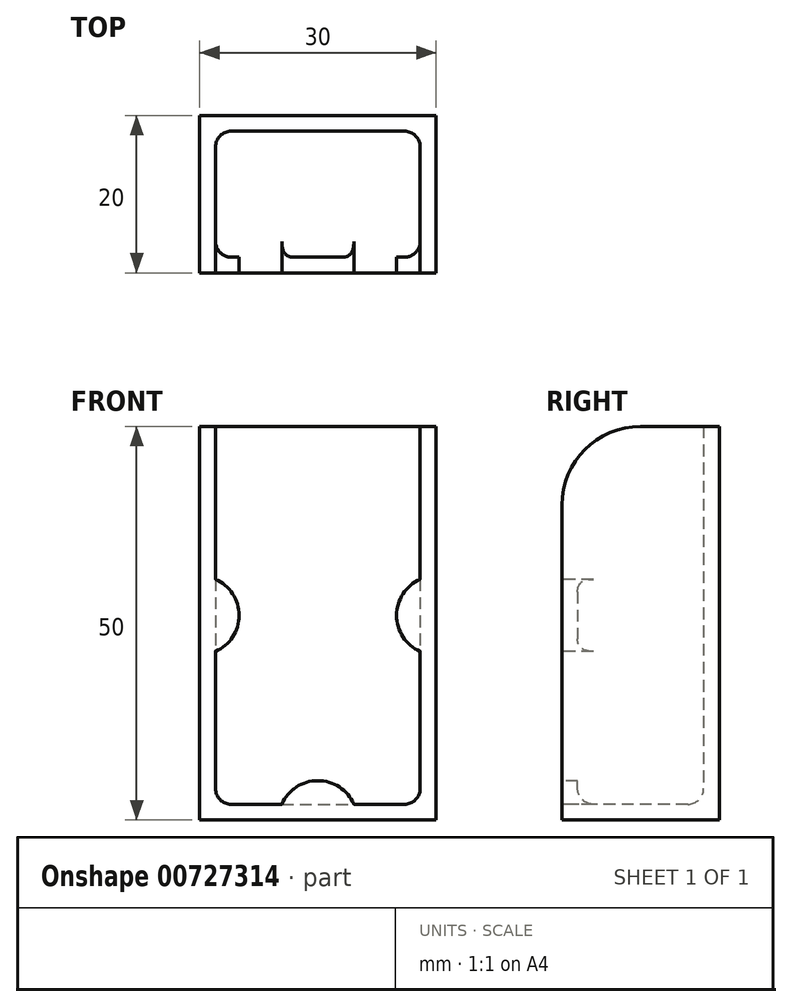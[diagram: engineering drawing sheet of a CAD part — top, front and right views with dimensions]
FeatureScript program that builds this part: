
annotation { "Feature Type Name" : "Feature", "Feature Type Description" : "" }
export const myFeature = defineFeature(function(context is Context, id is Id, definition is map)
    precondition{}
    {
        {
            var Q0;
            Q0=qCreatedBy(makeId("Top.planeOp"),FACE);
            var sketch = newSketch(context, id + "F0", { "sketchPlane" : qUnion([Q0])});
            skLineSegment(sketch, "E0.bottom", {"start": v(-15, 10) * mm, "end": v(15, 10) * mm});
            skLineSegment(sketch, "E0.top", {"start": v(-15, -10) * mm, "end": v(15, -10) * mm});
            skLineSegment(sketch, "E0.left", {"start": v(-15, 10) * mm, "end": v(-15, -10) * mm});
            skLineSegment(sketch, "E0.right", {"start": v(15, 10) * mm, "end": v(15, -10) * mm});
            skPoint(sketch, "E0.middle", {"position": v(0, 0) * mm});
            skLineSegment(sketch, "E1.bottom", {"start": v(-13, 8) * mm, "end": v(13, 8) * mm});
            skLineSegment(sketch, "E1.top", {"start": v(-13, -8) * mm, "end": v(13, -8) * mm});
            skLineSegment(sketch, "E1.left", {"start": v(-13, 8) * mm, "end": v(-13, -8) * mm});
            skLineSegment(sketch, "E1.right", {"start": v(13, 8) * mm, "end": v(13, -8) * mm});
            skSolve(sketch);
        }
        {
            var Q0;
            Q0=makeQuery(id+"F0.imprint","IMPRINT",FACE,{"disambiguationData":[TD([[makeQuery(id+"F0.imprint","IMPRINT",EDGE,{"derivedFrom":sQuery(id+"F0.wireOp",EDGE,"E0.bottom")}),-1.0]])]});
            extrude(context, id + "F1", {"entities" : qUnion([Q0]), "depth" : 50 * mm, "offsetDistance" : 25 * mm});
        }
        {
            var Q0;
            Q0=qCreatedBy(makeId("Top.planeOp"),FACE);
            var sketch = newSketch(context, id + "F2", { "sketchPlane" : qUnion([Q0])});
            skLineSegment(sketch, "E2.0", {"start": v(-15, 10) * mm, "end": v(-15, -10) * mm});
            skLineSegment(sketch, "E3.0", {"start": v(-15, -10) * mm, "end": v(15, -10) * mm});
            skLineSegment(sketch, "E4.0", {"start": v(15, 10) * mm, "end": v(15, -10) * mm});
            skLineSegment(sketch, "E5.0", {"start": v(-15, 10) * mm, "end": v(15, 10) * mm});
            skPoint(sketch, "E6.middle", {"position": v(0, 0) * mm});
            skSolve(sketch);
        }
        {
            var Q0;
            Q0=qSketchRegion(id+"F2",true);
            extrude(context, id + "F3", {"entities" : qUnion([Q0]), "operationType" : NewBodyOperationType.ADD, "depth" : 2 * mm, "offsetDistance" : 25 * mm});
        }
        {
            var Q0;
            Q0=makeQuery(id+"F1.opExtrude","SWEPT_FACE",FACE,{"disambiguationData":[OSD([sQuery(id+"F0.wireOp",EDGE,"E0.top")])]});
            var sketch = newSketch(context, id + "F4", { "sketchPlane" : qUnion([Q0])});
            skLineSegment(sketch, "E7.0", {"start": v(-13, 50) * mm, "end": v(13, 50) * mm});
            skLineSegment(sketch, "E8.0", {"start": v(-13, 2) * mm, "end": v(-4.58, 2) * mm});
            skLineSegment(sketch, "E9.0", {"start": v(13, 50) * mm, "end": v(13, 30.58) * mm});
            skLineSegment(sketch, "E10.0", {"start": v(-13, 50) * mm, "end": v(-13, 30.58) * mm});
            skArc(sketch, "E11", {"start": v(-13, 21.42) * mm, "mid": v(-10, 26) * mm, "end": v(-13, 30.58) * mm});
            skPoint(sketch, "E11.centerSnap0", {"position": v(-13, 26) * mm});
            skArc(sketch, "E12", {"start": v(4.58, 2) * mm, "mid": v(0, 5) * mm, "end": v(-4.58, 2) * mm});
            skArc(sketch, "E13", {"start": v(13, 30.58) * mm, "mid": v(10, 26) * mm, "end": v(13, 21.42) * mm});
            skPoint(sketch, "E13.centerSnap0", {"position": v(13, 26) * mm});
            skLineSegment(sketch, "E14.trimOffspring", {"start": v(13, 21.42) * mm, "end": v(13, 2) * mm});
            skLineSegment(sketch, "E15.trimOffspring", {"start": v(-13, 21.42) * mm, "end": v(-13, 2) * mm});
            skPoint(sketch, "E16.orphan", {"position": v(15, 50) * mm});
            skLineSegment(sketch, "E17.trimOffspring", {"start": v(4.58, 2) * mm, "end": v(13, 2) * mm});
            skPoint(sketch, "E18.0.end.orphan", {"position": v(15, 0) * mm});
            skPoint(sketch, "E19.orphan", {"position": v(-15, 0) * mm});
            skPoint(sketch, "E20.orphan", {"position": v(-15, 50) * mm});
            skSolve(sketch);
        }
        {
            var Q0;
            Q0=makeQuery(id+"F4.imprint","IMPRINT",FACE,{"disambiguationData":[TD([[makeQuery(id+"F4.imprint","IMPRINT",EDGE,{"derivedFrom":sQuery(id+"F4.wireOp",EDGE,"E7.0")}),-1.0]])]});
            extrude(context, id + "F5", {"entities" : qUnion([Q0]), "operationType" : NewBodyOperationType.REMOVE, "endBound" : BoundingType.UP_TO_NEXT, "oppositeDirection" : true, "depth" : 25 * mm, "offsetDistance" : 25 * mm});
        }
        {
            var Q0;
            {var subQ1=sQuery(id+"F0.wireOp",EDGE,"E0.right");var subQ2=sQuery(id+"F0.wireOp",EDGE,"E0.top");Q0=makeQuery(id+"F5.boolean.opBoolean","SPLIT",EDGE,{"disambiguationData":[TD([makeQuery(id+"F1.opExtrude","SWEPT_FACE",FACE,{"disambiguationData":[OSD([subQ1])]})])],"derivedFrom":makeQuery(id+"F1.opExtrude","CAP_EDGE",EDGE,{"disambiguationData":[OSD([subQ2])],"isStart":false})});}
            var Q1;
            {var subQ0=sQuery(id+"F0.wireOp",EDGE,"E0.left");var subQ2=sQuery(id+"F0.wireOp",EDGE,"E0.top");Q1=makeQuery(id+"F5.boolean.opBoolean","SPLIT",EDGE,{"disambiguationData":[TD([makeQuery(id+"F1.opExtrude","SWEPT_FACE",FACE,{"disambiguationData":[OSD([subQ0])]})])],"derivedFrom":makeQuery(id+"F1.opExtrude","CAP_EDGE",EDGE,{"disambiguationData":[OSD([subQ2])],"isStart":false})});}
            fillet(context, id + "F6", {"entities" : qUnion([Q0, Q1]), "radius" : 10 * mm, "tangentPropagation" : true, "allowEdgeOverflow" : false});
        }
        {
            var Q0;
            Q0=makeQuery(id+"F5.boolean.opBoolean","MERGE",EDGE,{"derivedFrom":[makeQuery(id+"F3.boolean.opBoolean","INTERSECT",EDGE,{"derivedFrom":[makeQuery(id+"F1.opExtrude","SWEPT_FACE",FACE,{"disambiguationData":[OSD([sQuery(id+"F0.wireOp",EDGE,"E1.right")])]}),makeQuery(id+"F3.opExtrude","CAP_FACE",FACE,{"disambiguationData":[OSD([sQuery(id+"F2.wireOp",EDGE,"E5.0"),sQuery(id+"F2.wireOp",EDGE,"E3.0"),sQuery(id+"F2.wireOp",EDGE,"E2.0"),sQuery(id+"F2.wireOp",EDGE,"E4.0")])],"isStart":false})]}),makeQuery(id+"F5.opExtrude","SWEPT_EDGE",EDGE,{"disambiguationData":[OSD([sQuery(id+"F4.wireOp",EDGE,"E14.trimOffspring"),sQuery(id+"F4.wireOp",EDGE,"E17.trimOffspring")])]})]});
            var Q1;
            Q1=makeQuery(id+"F1.opExtrude","SWEPT_EDGE",EDGE,{"disambiguationData":[OSD([sQuery(id+"F0.wireOp",EDGE,"E1.bottom"),sQuery(id+"F0.wireOp",EDGE,"E1.right")])]});
            var Q2;
            Q2=makeQuery(id+"F3.boolean.opBoolean","INTERSECT",EDGE,{"derivedFrom":[makeQuery(id+"F1.opExtrude","SWEPT_FACE",FACE,{"disambiguationData":[OSD([sQuery(id+"F0.wireOp",EDGE,"E1.bottom")])]}),makeQuery(id+"F3.opExtrude","CAP_FACE",FACE,{"disambiguationData":[OSD([sQuery(id+"F2.wireOp",EDGE,"E5.0"),sQuery(id+"F2.wireOp",EDGE,"E3.0"),sQuery(id+"F2.wireOp",EDGE,"E2.0"),sQuery(id+"F2.wireOp",EDGE,"E4.0")])],"isStart":false})]});
            var Q3;
            {var subQ0=sQuery(id+"F2.wireOp",EDGE,"E4.0");var subQ1=sQuery(id+"F2.wireOp",EDGE,"E2.0");var subQ2=sQuery(id+"F2.wireOp",EDGE,"E3.0");var subQ3=sQuery(id+"F2.wireOp",EDGE,"E5.0");var subQ4=sQuery(id+"F0.wireOp",EDGE,"E1.left");Q3=makeQuery(id+"F5.boolean.opBoolean","MERGE",EDGE,{"derivedFrom":[makeQuery(id+"F3.boolean.opBoolean","INTERSECT",EDGE,{"derivedFrom":[makeQuery(id+"F1.opExtrude","SWEPT_FACE",FACE,{"disambiguationData":[OSD([subQ4])]}),makeQuery(id+"F3.opExtrude","CAP_FACE",FACE,{"disambiguationData":[OSD([subQ3,subQ2,subQ1,subQ0])],"isStart":false})]}),makeQuery(id+"F5.opExtrude","SWEPT_EDGE",EDGE,{"disambiguationData":[OSD([sQuery(id+"F0.wireOp",EDGE,"E1.top"),subQ4,subQ3,subQ2,subQ1,subQ0])]})]});}
            var Q4;
            Q4=makeQuery(id+"F1.opExtrude","SWEPT_EDGE",EDGE,{"disambiguationData":[OSD([sQuery(id+"F0.wireOp",EDGE,"E1.bottom"),sQuery(id+"F0.wireOp",EDGE,"E1.left")])]});
            var Q5;
            Q5=makeQuery(id+"F1.opExtrude","SWEPT_EDGE",EDGE,{"disambiguationData":[OSD([sQuery(id+"F0.wireOp",EDGE,"E1.top"),sQuery(id+"F0.wireOp",EDGE,"E1.right")])]});
            var Q6;
            Q6=makeQuery(id+"F1.opExtrude","SWEPT_EDGE",EDGE,{"disambiguationData":[OSD([sQuery(id+"F0.wireOp",EDGE,"E1.top"),sQuery(id+"F0.wireOp",EDGE,"E1.left")])]});
            var Q7;
            Q7=makeQuery(id+"F3.boolean.opBoolean","INTERSECT",EDGE,{"derivedFrom":[makeQuery(id+"F1.opExtrude","SWEPT_FACE",FACE,{"disambiguationData":[OSD([sQuery(id+"F0.wireOp",EDGE,"E1.top")])]}),makeQuery(id+"F3.opExtrude","CAP_FACE",FACE,{"disambiguationData":[OSD([sQuery(id+"F2.wireOp",EDGE,"E5.0"),sQuery(id+"F2.wireOp",EDGE,"E3.0"),sQuery(id+"F2.wireOp",EDGE,"E2.0"),sQuery(id+"F2.wireOp",EDGE,"E4.0")])],"isStart":false})]});
            fillet(context, id + "F7", {"entities" : qUnion([Q0, Q1, Q2, Q3, Q4, Q5, Q6, Q7]), "radius" : 2 * mm, "tangentPropagation" : true, "allowEdgeOverflow" : false});
        }
    });
